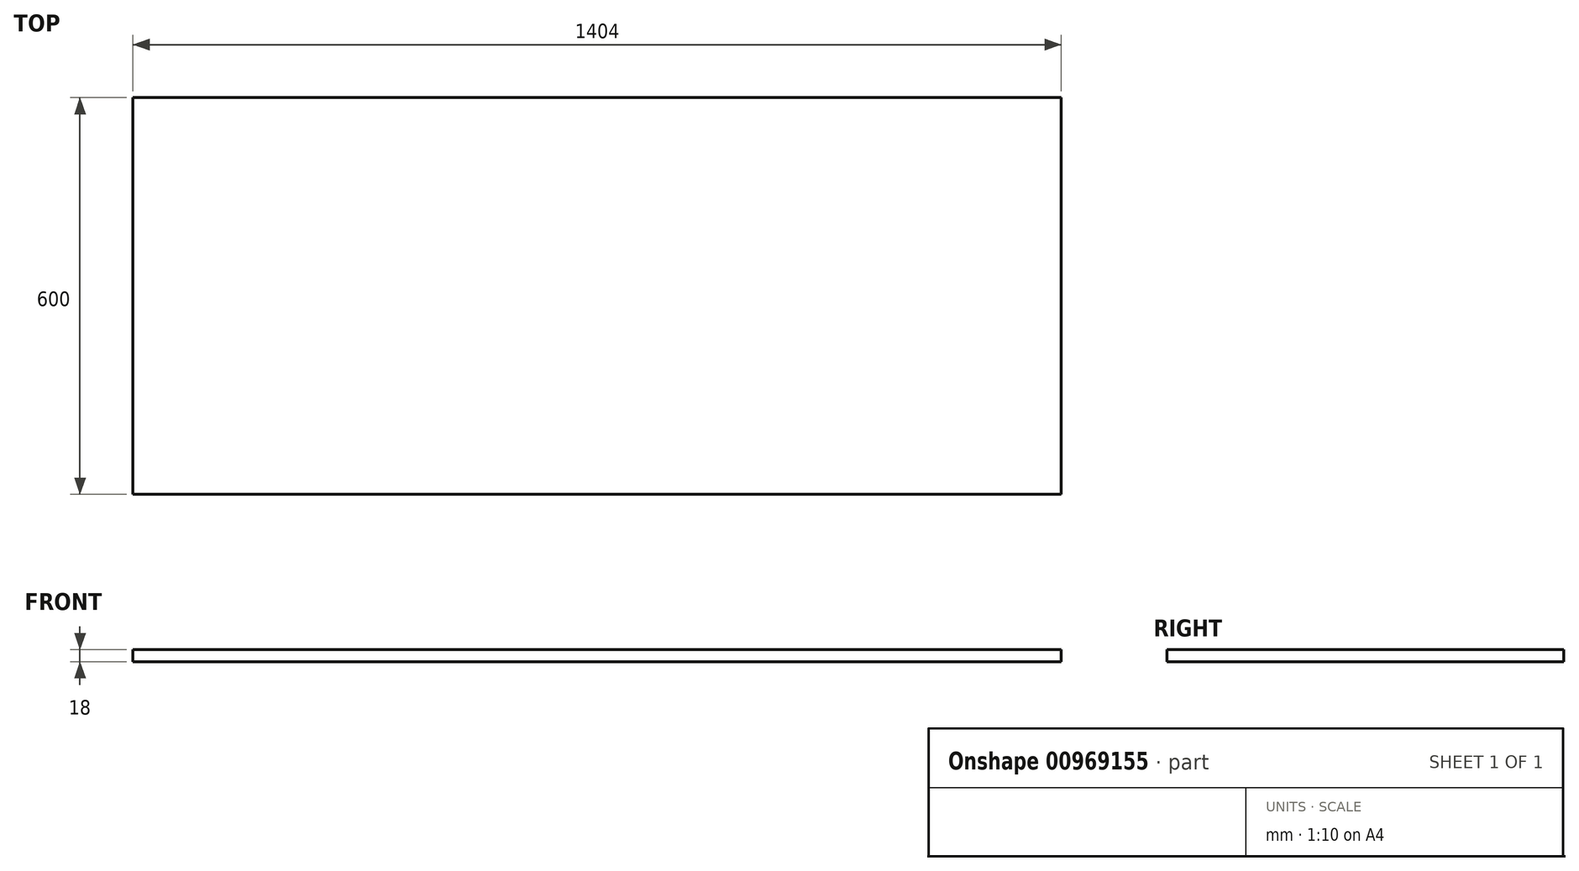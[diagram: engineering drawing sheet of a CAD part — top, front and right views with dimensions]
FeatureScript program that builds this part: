
annotation { "Feature Type Name" : "Feature", "Feature Type Description" : "" }
export const myFeature = defineFeature(function(context is Context, id is Id, definition is map)
    precondition{}
    {
        {
            var Q0;
            Q0=qCreatedBy(makeId("Top.planeOp"),FACE);
            var sketch = newSketch(context, id + "F0", { "sketchPlane" : qUnion([Q0])});
            skLineSegment(sketch, "E0.bottom", {"start": v(0, 0) * mm, "end": v(1404, 0) * mm});
            skLineSegment(sketch, "E0.top", {"start": v(0, 600) * mm, "end": v(1404, 600) * mm});
            skLineSegment(sketch, "E0.left", {"start": v(0, 0) * mm, "end": v(0, 600) * mm});
            skLineSegment(sketch, "E0.right", {"start": v(1404, 0) * mm, "end": v(1404, 600) * mm});
            skSolve(sketch);
        }
        {
            var Q0;
            Q0 = qSketchRegion(id + "F0", true);
            extrude(context, id + "F1", {"entities" : qUnion([Q0]), "depth" : 18 * mm, "offsetDistance" : 25 * mm});
        }
    });
